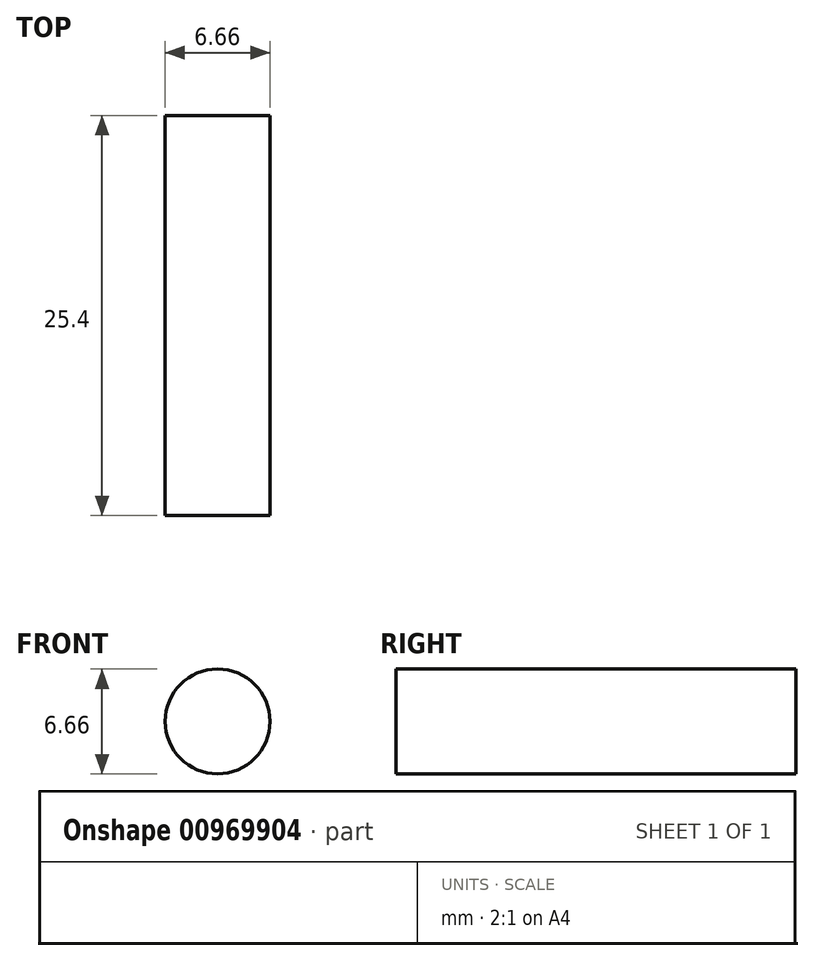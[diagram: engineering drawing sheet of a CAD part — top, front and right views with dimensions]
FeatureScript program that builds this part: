
annotation { "Feature Type Name" : "Feature", "Feature Type Description" : "" }
export const myFeature = defineFeature(function(context is Context, id is Id, definition is map)
    precondition{}
    {
        {
            var Q0;
            Q0=qCreatedBy(makeId("Front.planeOp"),FACE);
            var sketch = newSketch(context, id + "F0", { "sketchPlane" : qUnion([Q0])});
            skCircle(sketch, "E0", {"center": v(33.1, 38.72) * mm, "radius": 3.33 * mm});
            skSolve(sketch);
        }
        {
            var Q0;
            Q0=sQuery(id+"F0.wireOp",EDGE,"E0");
            extrude(context, id + "F1", {"bodyType" : ToolBodyType.SURFACE, "surfaceEntities" : qUnion([Q0]), "depth" : 25.4 * mm, "offsetDistance" : 25.4 * mm});
        }
    });
